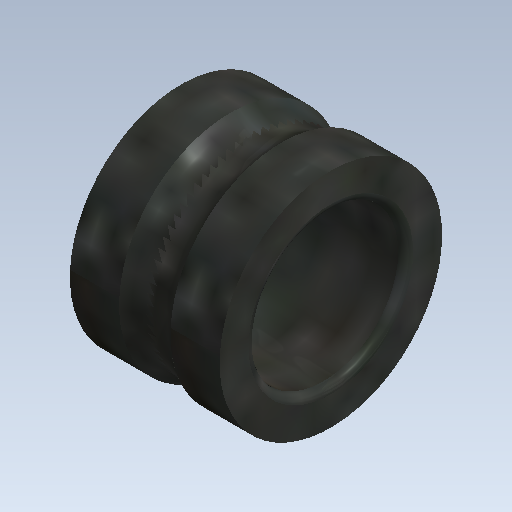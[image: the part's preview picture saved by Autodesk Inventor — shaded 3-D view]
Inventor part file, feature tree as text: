
AUTODESK INVENTOR PART (.ipt)
format: ipt  version: 2021 (Build 250183000, 183)  size: 208,384 bytes
history: native  units: mm (DEFAULTED — no unit token found)
features: other x63, revolve x1, sketch x1
ambient origin geometry x8: Origin, YZ Plane, XZ Plane, XY Plane, X Axis, Y Axis, Z Axis, Center Point
bodies: Solid1 (feature_tree)
feature tree (65):
  revolve  "Revolution1"  [1 undecoded]
  other  "ip_op_ir_1_1_XY"
  other  "ip_op_ir_1_1_YZ"
  other  "ip_op_ir_1_1_ZX"
  other  "ip_op_ir_1_1_X"
  other  "ip_op_ir_1_1_Y"
  other  "ip_op_ir_1_1_Z"
  other  "ip_op_ir_1_1_Center"
  other  "ip_op_ir_1_2_XY"
  other  "ip_op_ir_1_2_YZ"
  other  "ip_op_ir_1_2_ZX"
  other  "ip_op_ir_1_2_X"
  other  "ip_op_ir_1_2_Y"
  other  "ip_op_ir_1_2_Z"
  other  "ip_op_ir_1_2_Center"
  other  "ip_op_ir_1_3_XY"
  other  "ip_op_ir_1_3_YZ"
  other  "ip_op_ir_1_3_ZX"
  other  "ip_op_ir_1_3_X"
  other  "ip_op_ir_1_3_Y"
  other  "ip_op_ir_1_3_Z"
  other  "ip_op_ir_1_3_Center"
  other  "ip_op_ir_1_4_XY"
  other  "ip_op_ir_1_4_YZ"
  other  "ip_op_ir_1_4_ZX"
  other  "ip_op_ir_1_4_X"
  other  "ip_op_ir_1_4_Y"
  other  "ip_op_ir_1_4_Z"
  other  "ip_op_ir_1_4_Center"
  other  "ip_op_ir_1_5_XY"
  other  "ip_op_ir_1_5_YZ"
  other  "ip_op_ir_1_5_ZX"
  other  "ip_op_ir_1_5_X"
  other  "ip_op_ir_1_5_Y"
  other  "ip_op_ir_1_5_Z"
  other  "ip_op_ir_1_5_Center"
  other  "ip_op_ir_1_6_XY"
  other  "ip_op_ir_1_6_YZ"
  other  "ip_op_ir_1_6_ZX"
  other  "ip_op_ir_1_6_X"
  other  "ip_op_ir_1_6_Y"
  other  "ip_op_ir_1_6_Z"
  other  "ip_op_ir_1_6_Center"
  other  "ip_op_ir_1_7_XY"
  other  "ip_op_ir_1_7_YZ"
  other  "ip_op_ir_1_7_ZX"
  other  "ip_op_ir_1_7_X"
  other  "ip_op_ir_1_7_Y"
  other  "ip_op_ir_1_7_Z"
  other  "ip_op_ir_1_7_Center"
  other  "ip_op_ir_1_8_XY"
  other  "ip_op_ir_1_8_YZ"
  other  "ip_op_ir_1_8_ZX"
  other  "ip_op_ir_1_8_X"
  other  "ip_op_ir_1_8_Y"
  other  "ip_op_ir_1_8_Z"
  other  "ip_op_ir_1_8_Center"
  other  "ip_op_ir_1a_XY"
  other  "ip_op_ir_1a_YZ"
  other  "ip_op_ir_1a_ZX"
  other  "ip_op_ir_1a_X"
  other  "ip_op_ir_1a_Y"
  other  "ip_op_ir_1a_Z"
  other  "ip_op_ir_1a_Center"
  sketch  "Sketch_1"  dims[d0=360.0deg d1=0.0mm]
note: 1 required parameter value undecoded (feature->parameter linkage not recoverable at this tier; creation-order binding heuristic only, values carry confidence <= 0.55)
